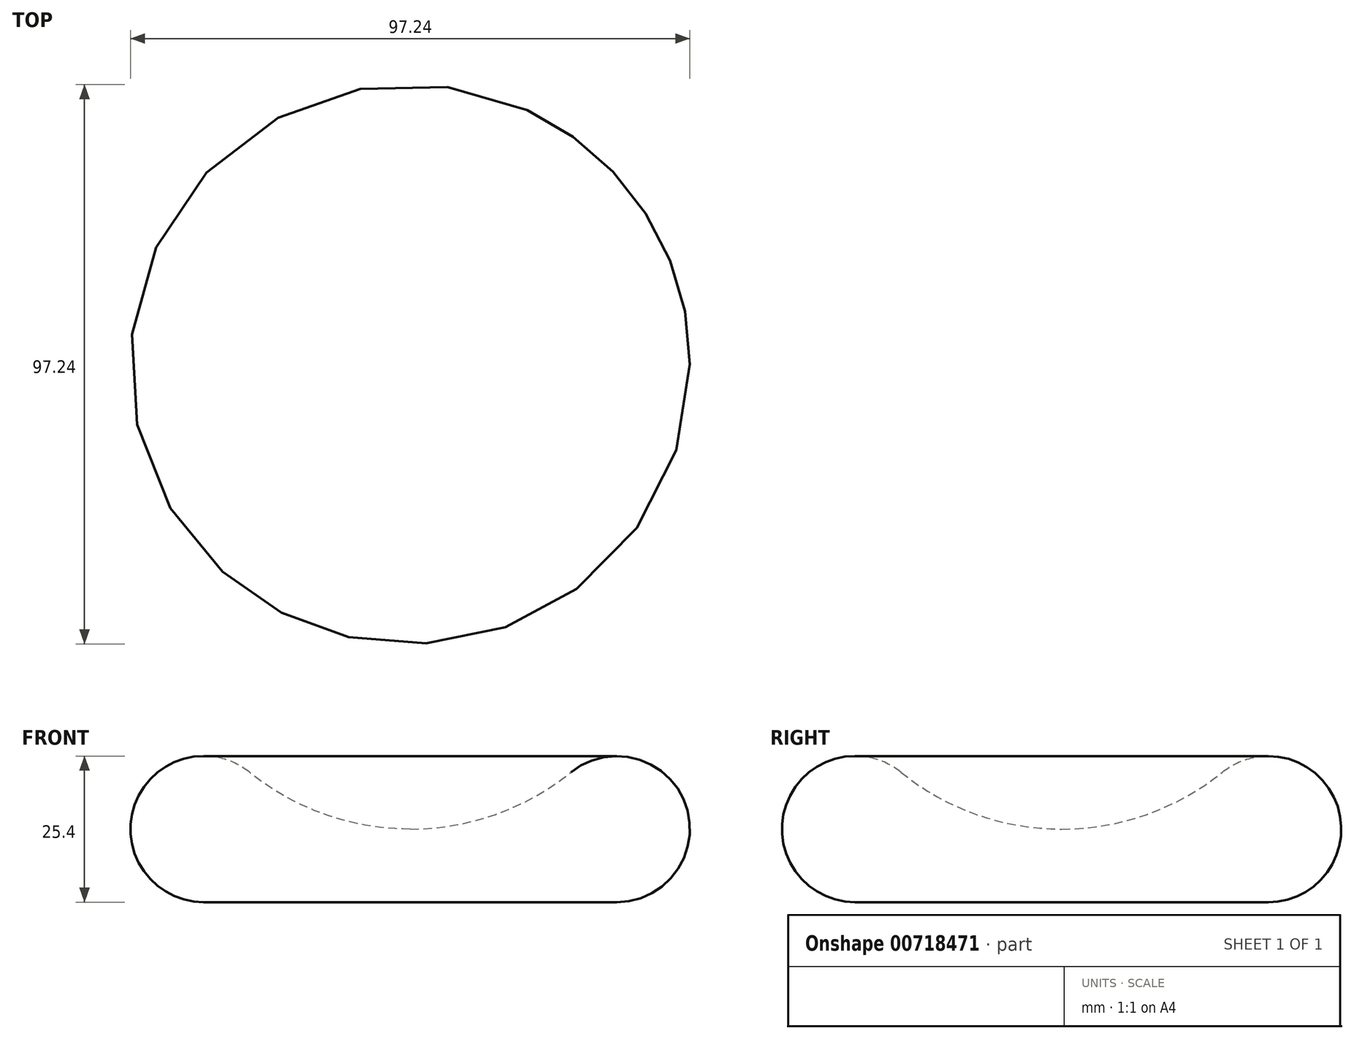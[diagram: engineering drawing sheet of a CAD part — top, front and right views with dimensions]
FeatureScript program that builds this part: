
annotation { "Feature Type Name" : "Feature", "Feature Type Description" : "" }
export const myFeature = defineFeature(function(context is Context, id is Id, definition is map)
    precondition{}
    {
        {
            var Q0;
            Q0=qCreatedBy(makeId("Front.planeOp"),FACE);
            var sketch = newSketch(context, id + "F0", { "sketchPlane" : qUnion([Q0])});
            skArc(sketch, "E0", {"start": v(-27.94, 22.58) * mm, "mid": v(-47.9, 16.93) * mm, "end": v(-35.92, 0) * mm});
            skArc(sketch, "E1", {"start": v(-27.94, 22.58) * mm, "mid": v(-14.82, 15.24) * mm, "end": v(0, 12.7) * mm});
            skLineSegment(sketch, "E2", {"start": v(-35.92, 0) * mm, "end": v(0, 0) * mm});
            skPoint(sketch, "E3.orphan", {"position": v(-78.87, 0) * mm});
            skLineSegment(sketch, "E4.trimOffspring", {"start": v(0, 12.7) * mm, "end": v(0, 0) * mm});
            skPoint(sketch, "E5.start.orphan", {"position": v(0, 101.6) * mm});
            skSolve(sketch);
        }
        {
            var Q0;
            Q0=makeQuery(id+"F0.imprint","IMPRINT",FACE,{"disambiguationData":[TD([[makeQuery(id+"F0.imprint","IMPRINT",EDGE,{"derivedFrom":sQuery(id+"F0.wireOp",EDGE,"E0")}),1.0]])]});
            var Q1;
            Q1=sQuery(id+"F0.wireOp",EDGE,"E4.trimOffspring");
            revolve(context, id + "F1", {"surfaceOperationType" : NewSurfaceOperationType.NEW, "entities" : qUnion([Q0]), "axis" : qUnion([Q1]), "revolveType" : RevolveType.FULL});
        }
    });
